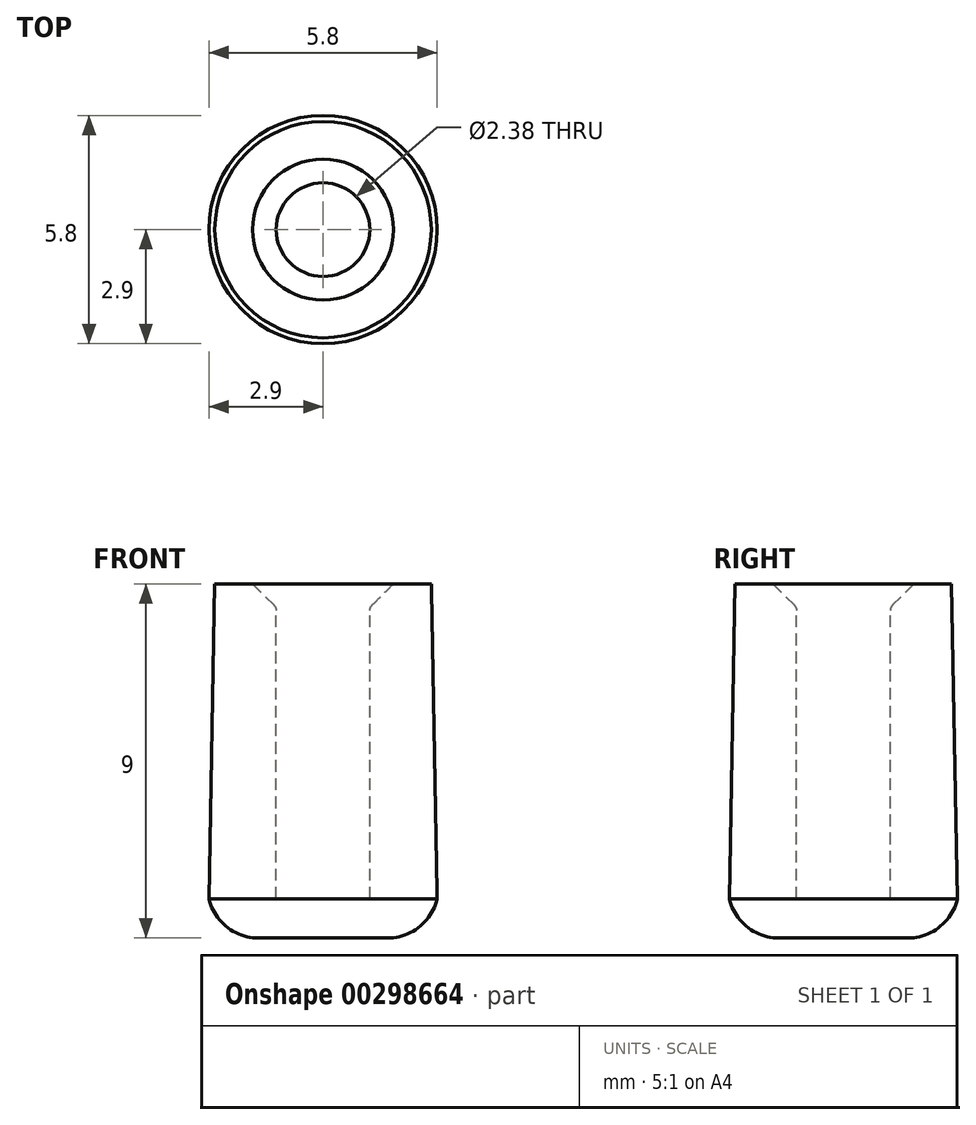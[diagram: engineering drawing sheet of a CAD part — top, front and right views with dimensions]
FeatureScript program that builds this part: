
annotation { "Feature Type Name" : "Feature", "Feature Type Description" : "" }
export const myFeature = defineFeature(function(context is Context, id is Id, definition is map)
    precondition{}
    {
        {
            var Q0;
            Q0=qCreatedBy(makeId("Top.planeOp"),FACE);
            var sketch = newSketch(context, id + "F0", { "sketchPlane" : qUnion([Q0])});
            skCircle(sketch, "E0", {"center": v(0, 0) * mm, "radius": 2.9 * mm});
            skSolve(sketch);
        }
        {
            var Q0;
            Q0=makeQuery(id+"F0.imprint","IMPRINT",FACE,{"disambiguationData":[TD([[makeQuery(id+"F0.imprint","IMPRINT",EDGE,{"derivedFrom":sQuery(id+"F0.wireOp",EDGE,"E0")}),1.0]])]});
            extrude(context, id + "F1", {"entities" : qUnion([Q0]), "depth" : 1 * mm});
        }
        {
            var Q0;
            Q0=qCreatedBy(makeId("Front.planeOp"),FACE);
            var sketch = newSketch(context, id + "F2", { "sketchPlane" : qUnion([Q0])});
            skLineSegment(sketch, "E1", {"start": v(0, 0) * mm, "end": v(0, 1) * mm});
            skLineSegment(sketch, "E2", {"start": v(0, 1) * mm, "end": v(-2.9, 1) * mm});
            skLineSegment(sketch, "E3", {"start": v(-2.9, 1) * mm, "end": v(-2.75, 9) * mm});
            skLineSegment(sketch, "E4", {"start": v(-2.75, 9) * mm, "end": v(0, 9) * mm});
            skLineSegment(sketch, "E5", {"start": v(0, 9) * mm, "end": v(0, 1) * mm});
            skLineSegment(sketch, "E6", {"start": v(0, 9) * mm, "end": v(-1.19, 9) * mm});
            skLineSegment(sketch, "E7", {"start": v(-1.19, 9) * mm, "end": v(-1.19, 1) * mm});
            skLineSegment(sketch, "E8", {"start": v(0, 9) * mm, "end": v(-0.6, 9) * mm});
            skLineSegment(sketch, "E9", {"start": v(-0.6, 9) * mm, "end": v(0, 8.4) * mm});
            skLineSegment(sketch, "E10", {"start": v(0, 8.4) * mm, "end": v(0, 9) * mm});
            skSolve(sketch);
        }
        {
            var Q0;
            {var subQ0=sQuery(id+"F2.wireOp",EDGE,"E3");Q0=makeQuery(id+"F2.imprint","IMPRINT",FACE,{"disambiguationData":[TD([[makeQuery(id+"F2.imprint","IMPRINT",EDGE,{"derivedFrom":subQ0}),-1.0]])]});}
            var Q1;
            Q1=sQuery(id+"F2.wireOp",EDGE,"E5");
            revolve(context, id + "F3", {"entities" : qUnion([Q0]), "axis" : qUnion([Q1]), "revolveType" : RevolveType.FULL});
        }
        {
            var Q0;
            Q0=makeQuery(id+"F1.opExtrude","CAP_EDGE",EDGE,{"disambiguationData":[OSD([sQuery(id+"F0.wireOp",EDGE,"E0")])],"isStart":true});
            fillet(context, id + "F4", {"entities" : qUnion([Q0]), "radius" : 1.3 * mm, "tangentPropagation" : true, "allowEdgeOverflow" : false});
        }
        {
            var Q0;
            Q0=makeQuery(id+"F3.opRevolve","SWEPT_EDGE",EDGE,{"disambiguationData":[OSD([sQuery(id+"F2.wireOp",EDGE,"E4"),sQuery(id+"F2.wireOp",EDGE,"E6"),sQuery(id+"F2.wireOp",EDGE,"E7")])]});
            chamfer(context, id + "F5", {"entities" : qUnion([Q0]), "width" : 0.6 * mm, "tangentPropagation" : true});
        }
        {
            var Q0;
            {var subQ0=sQuery(id+"F2.wireOp",EDGE,"E7");Q0=makeQuery(id+"F5.opChamfer","BLEND_EDGE",EDGE,{"blendedFrom":[makeQuery(id+"F3.opRevolve","SWEPT_EDGE",EDGE,{"disambiguationData":[OSD([sQuery(id+"F2.wireOp",EDGE,"E4"),sQuery(id+"F2.wireOp",EDGE,"E6"),subQ0])]}),makeQuery(id+"F3.opRevolve","SWEPT_FACE",FACE,{"disambiguationData":[OSD([subQ0])]})],"blendedInto":[makeQuery(id+"F3.opRevolve","SWEPT_FACE",FACE,{"disambiguationData":[OSD([subQ0])]})]});}
            fillet(context, id + "F6", {"entities" : qUnion([Q0]), "radius" : 0.2 * mm, "tangentPropagation" : true, "allowEdgeOverflow" : false});
        }
    });
